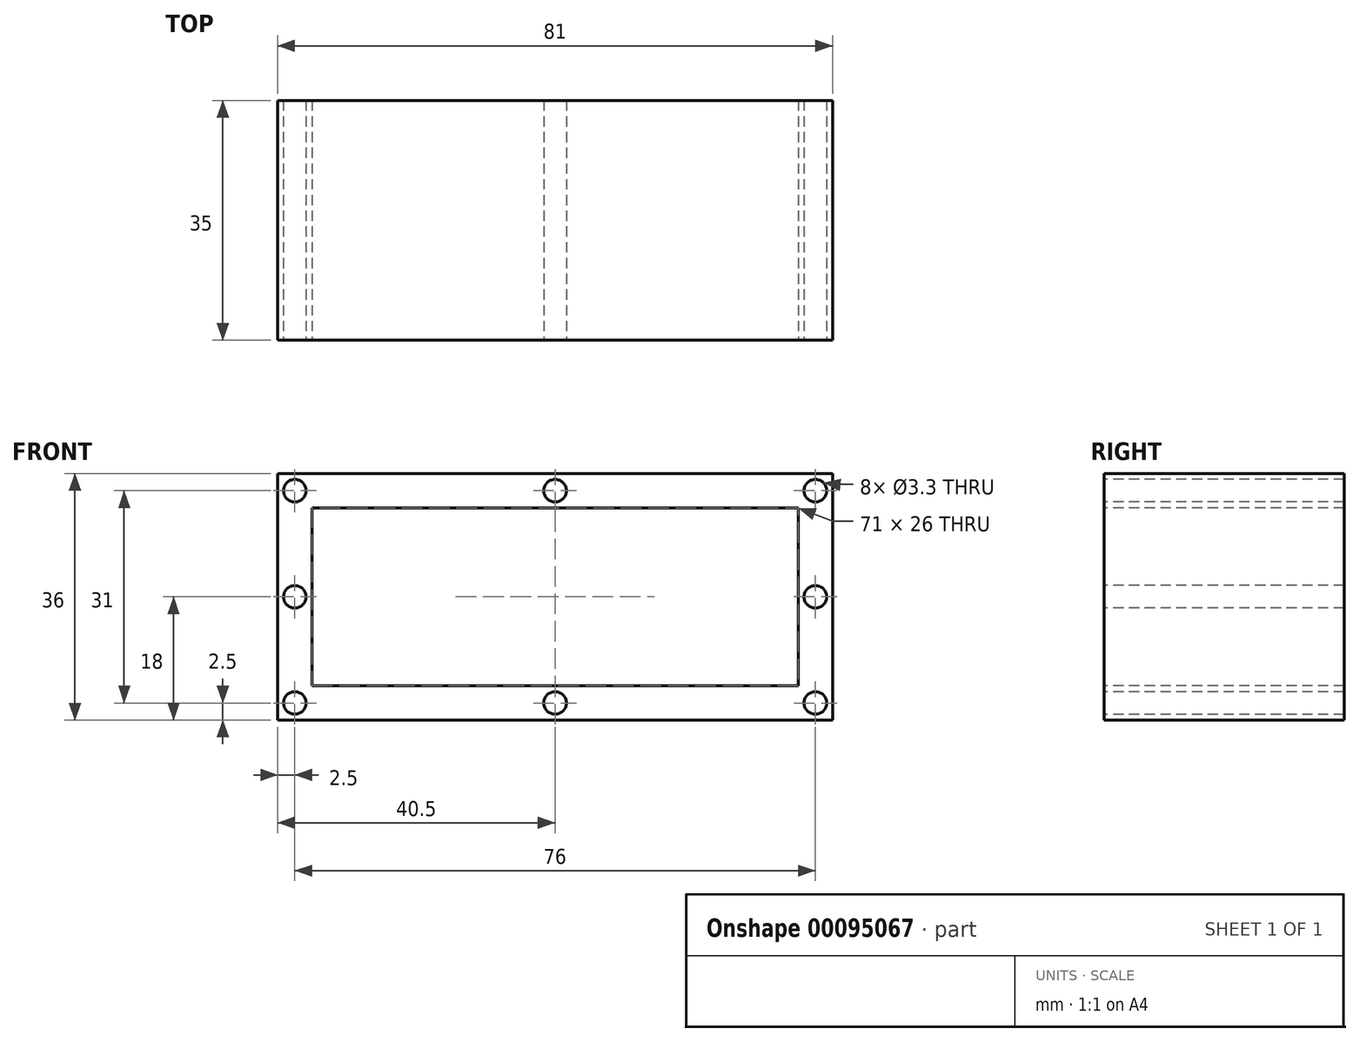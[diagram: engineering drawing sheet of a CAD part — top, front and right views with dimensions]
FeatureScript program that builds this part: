
annotation { "Feature Type Name" : "Feature", "Feature Type Description" : "" }
export const myFeature = defineFeature(function(context is Context, id is Id, definition is map)
    precondition{}
    {
        {
            var Q0;
            Q0=qCreatedBy(makeId("Front.planeOp"),FACE);
            var sketch = newSketch(context, id + "F0", { "sketchPlane" : qUnion([Q0])});
            skLineSegment(sketch, "E0.bottom", {"start": v(40.5, -18) * mm, "end": v(-40.5, -18) * mm});
            skLineSegment(sketch, "E0.top", {"start": v(40.5, 18) * mm, "end": v(-40.5, 18) * mm});
            skLineSegment(sketch, "E0.left", {"start": v(40.5, -18) * mm, "end": v(40.5, 18) * mm});
            skLineSegment(sketch, "E0.right", {"start": v(-40.5, -18) * mm, "end": v(-40.5, 18) * mm});
            skPoint(sketch, "E0.middle", {"position": v(0, 0) * mm});
            skSolve(sketch);
        }
        {
            var Q0;
            Q0 = qSketchRegion(id + "F0", true);
            extrude(context, id + "F1", {"entities" : qUnion([Q0]), "depth" : 35 * mm});
        }
        {
            var Q0;
            Q0=makeQuery(id+"F1.opExtrude","CAP_FACE",FACE,{"disambiguationData":[OSD([sQuery(id+"F0.wireOp",EDGE,"E0.bottom"),sQuery(id+"F0.wireOp",EDGE,"E0.top"),sQuery(id+"F0.wireOp",EDGE,"E0.left"),sQuery(id+"F0.wireOp",EDGE,"E0.right")])],"isStart":false});
            var sketch = newSketch(context, id + "F2", { "sketchPlane" : qUnion([Q0])});
            skLineSegment(sketch, "E1.bottom", {"start": v(35.5, -13) * mm, "end": v(-35.5, -13) * mm});
            skLineSegment(sketch, "E1.top", {"start": v(35.5, 13) * mm, "end": v(-35.5, 13) * mm});
            skLineSegment(sketch, "E1.left", {"start": v(35.5, -13) * mm, "end": v(35.5, 13) * mm});
            skLineSegment(sketch, "E1.right", {"start": v(-35.5, -13) * mm, "end": v(-35.5, 13) * mm});
            skPoint(sketch, "E1.middle", {"position": v(0, 0) * mm});
            skSolve(sketch);
        }
        {
            var Q0;
            Q0 = qSketchRegion(id + "F2", true);
            extrude(context, id + "F3", {"entities" : qUnion([Q0]), "operationType" : NewBodyOperationType.REMOVE, "endBound" : BoundingType.THROUGH_ALL, "oppositeDirection" : true, "depth" : 25 * mm});
        }
        {
            var Q0;
            Q0=makeQuery(id+"F1.opExtrude","CAP_FACE",FACE,{"disambiguationData":[OSD([sQuery(id+"F0.wireOp",EDGE,"E0.bottom"),sQuery(id+"F0.wireOp",EDGE,"E0.top"),sQuery(id+"F0.wireOp",EDGE,"E0.left"),sQuery(id+"F0.wireOp",EDGE,"E0.right")])],"isStart":false});
            var sketch = newSketch(context, id + "F4", { "sketchPlane" : qUnion([Q0])});
            skPoint(sketch, "E2.middle", {"position": v(0, 0) * mm});
            skCircle(sketch, "E3", {"center": v(0, 15.5) * mm, "radius": 1.65 * mm});
            skCircle(sketch, "E4", {"center": v(38, 15.5) * mm, "radius": 1.65 * mm});
            skCircle(sketch, "E5", {"center": v(38, 0) * mm, "radius": 1.65 * mm});
            skCircle(sketch, "E6", {"center": v(38, -15.5) * mm, "radius": 1.65 * mm});
            skCircle(sketch, "E7", {"center": v(0, -15.5) * mm, "radius": 1.65 * mm});
            skCircle(sketch, "E8", {"center": v(-38, -15.5) * mm, "radius": 1.65 * mm});
            skCircle(sketch, "E9", {"center": v(-38, 0) * mm, "radius": 1.65 * mm});
            skCircle(sketch, "E10", {"center": v(-38, 15.5) * mm, "radius": 1.65 * mm});
            skSolve(sketch);
        }
        {
            var Q0;
            Q0 = qSketchRegion(id + "F4", true);
            extrude(context, id + "F5", {"entities" : qUnion([Q0]), "operationType" : NewBodyOperationType.REMOVE, "endBound" : BoundingType.THROUGH_ALL, "oppositeDirection" : true, "depth" : 25 * mm});
        }
    });
